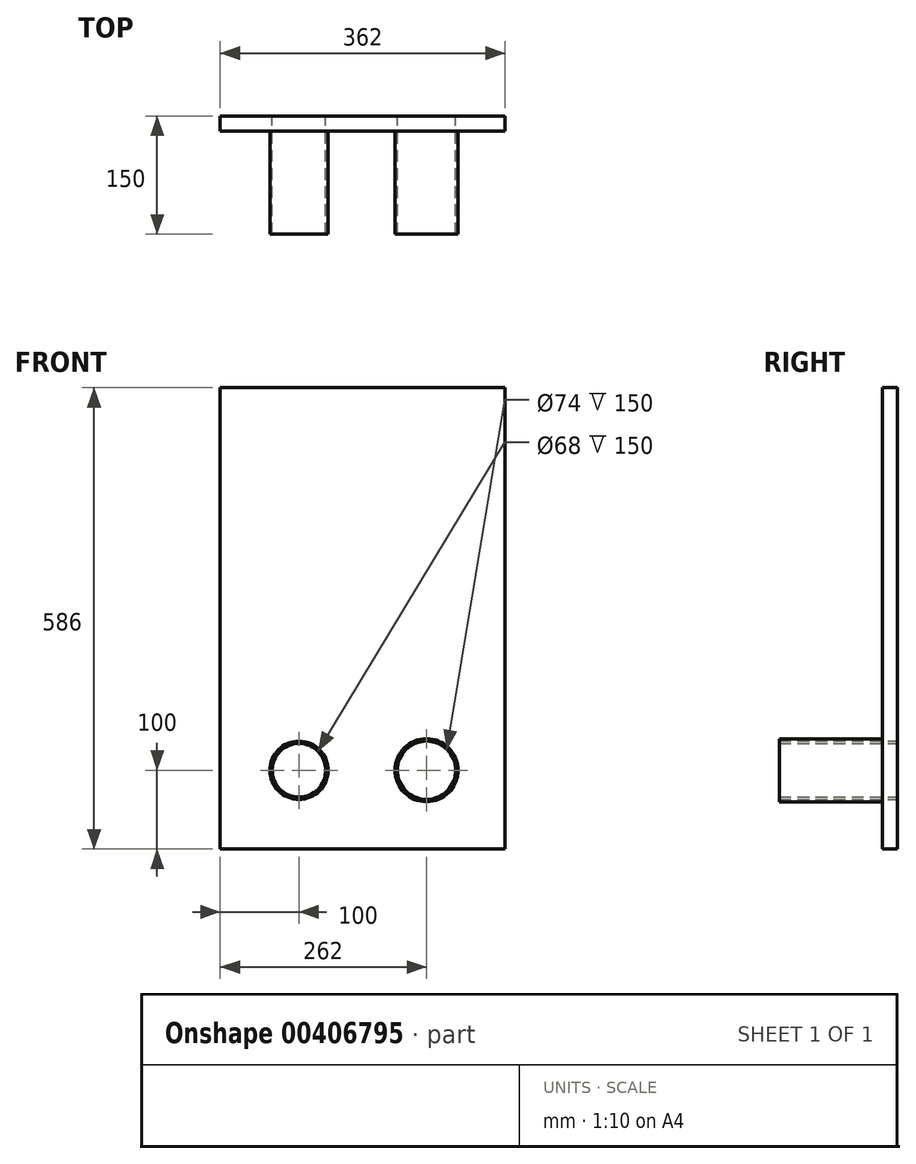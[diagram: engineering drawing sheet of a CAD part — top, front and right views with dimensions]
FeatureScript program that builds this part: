
annotation { "Feature Type Name" : "Feature", "Feature Type Description" : "" }
export const myFeature = defineFeature(function(context is Context, id is Id, definition is map)
    precondition{}
    {
        {
            var Q0;
            Q0=qCreatedBy(makeId("Front.planeOp"),FACE);
            var sketch = newSketch(context, id + "F0", { "sketchPlane" : qUnion([Q0])});
            skLineSegment(sketch, "E0.bottom", {"start": v(0, 0) * mm, "end": v(362, 0) * mm});
            skLineSegment(sketch, "E0.top", {"start": v(0, 586) * mm, "end": v(362, 586) * mm});
            skLineSegment(sketch, "E0.left", {"start": v(0, 0) * mm, "end": v(0, 586) * mm});
            skLineSegment(sketch, "E0.right", {"start": v(362, 0) * mm, "end": v(362, 586) * mm});
            skCircle(sketch, "E1", {"center": v(100, 100) * mm, "radius": 37 * mm});
            skCircle(sketch, "E2", {"center": v(262, 100) * mm, "radius": 37 * mm});
            skCircle(sketch, "E3.0", {"center": v(100, 100) * mm, "radius": 34 * mm});
            skCircle(sketch, "E4.0", {"center": v(262, 100) * mm, "radius": 40 * mm});
            skSolve(sketch);
        }
        {
            var Q0;
            Q0=makeQuery(id+"F0.imprint","IMPRINT",FACE,{"disambiguationData":[TD([[makeQuery(id+"F0.imprint","IMPRINT",EDGE,{"derivedFrom":sQuery(id+"F0.wireOp",EDGE,"E0.bottom")}),1.0]])]});
            extrude(context, id + "F1", {"entities" : qUnion([Q0]), "depth" : 19 * mm});
        }
        {
            var Q0;
            Q0=makeQuery(id+"F0.imprint","IMPRINT",FACE,{"disambiguationData":[TD([[makeQuery(id+"F0.imprint","IMPRINT",EDGE,{"derivedFrom":sQuery(id+"F0.wireOp",EDGE,"E2")}),-1.0]])]});
            extrude(context, id + "F2", {"entities" : qUnion([Q0]), "operationType" : NewBodyOperationType.ADD, "depth" : 150 * mm, "offsetDistance" : 25 * mm});
        }
        {
            var Q0;
            Q0=makeQuery(id+"F0.imprint","IMPRINT",FACE,{"disambiguationData":[TD([[makeQuery(id+"F0.imprint","IMPRINT",EDGE,{"derivedFrom":sQuery(id+"F0.wireOp",EDGE,"E1")}),1.0]])]});
            extrude(context, id + "F3", {"entities" : qUnion([Q0]), "operationType" : NewBodyOperationType.ADD, "depth" : 150 * mm});
        }
    });
